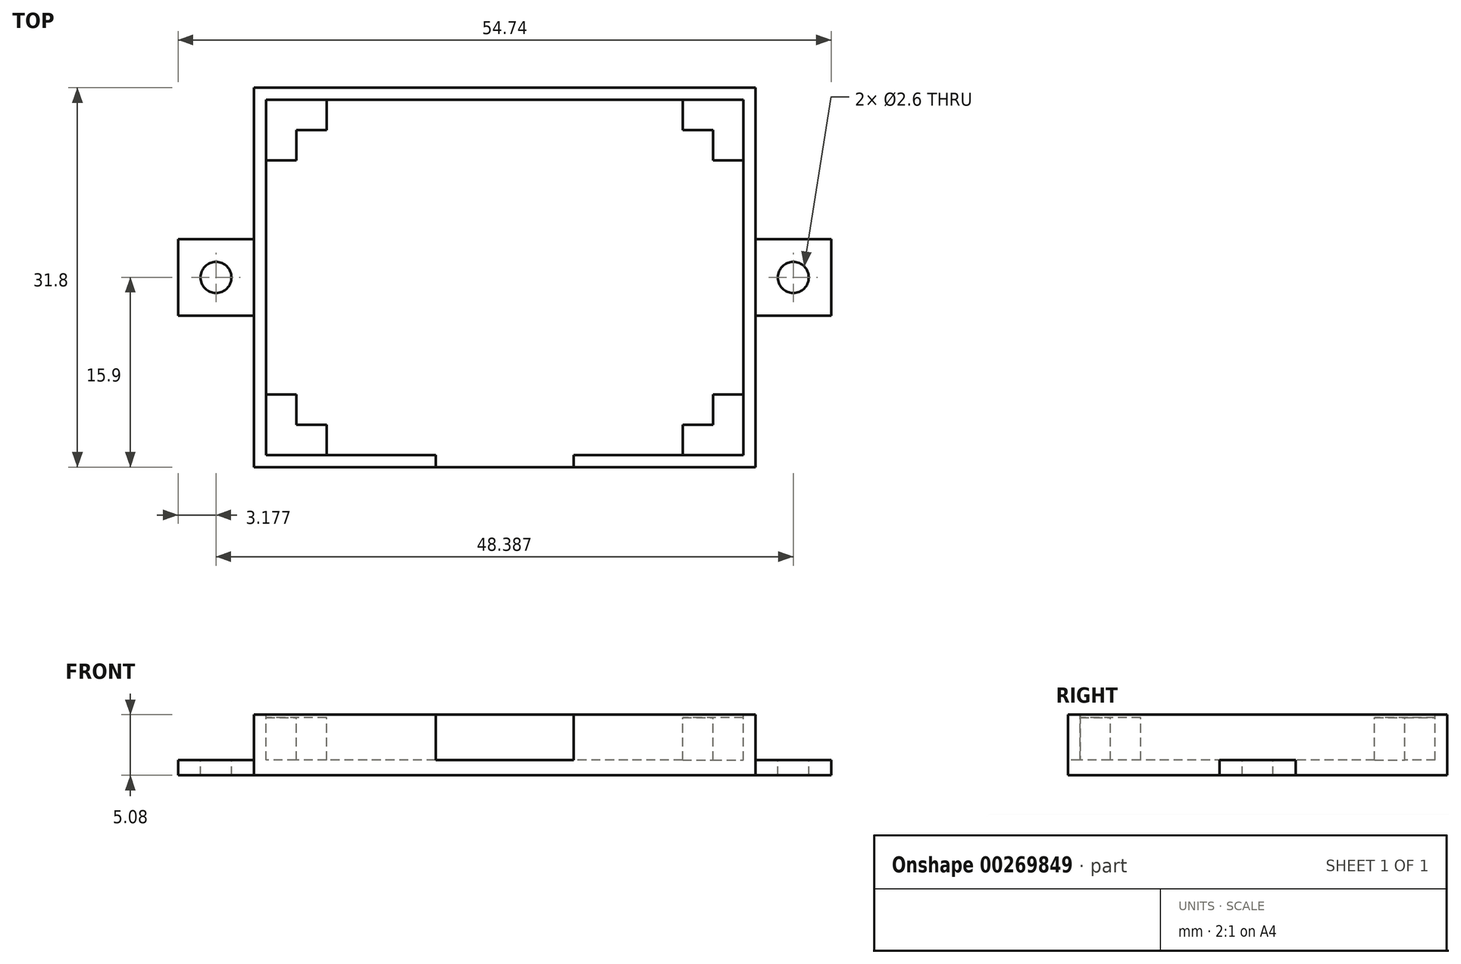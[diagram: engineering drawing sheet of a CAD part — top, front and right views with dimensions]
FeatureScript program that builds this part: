
annotation { "Feature Type Name" : "Feature", "Feature Type Description" : "" }
export const myFeature = defineFeature(function(context is Context, id is Id, definition is map)
    precondition{}
    {
        {
            var Q0;
            Q0=qCreatedBy(makeId("Top.planeOp"),FACE);
            var sketch = newSketch(context, id + "F0", { "sketchPlane" : qUnion([Q0])});
            skLineSegment(sketch, "E0.bottom", {"start": v(21.02, 15.9) * mm, "end": v(-21.02, 15.9) * mm});
            skLineSegment(sketch, "E0.top", {"start": v(21.02, -15.9) * mm, "end": v(-21.02, -15.9) * mm});
            skLineSegment(sketch, "E0.left", {"start": v(21.02, 15.9) * mm, "end": v(21.02, -15.9) * mm});
            skLineSegment(sketch, "E0.right", {"start": v(-21.02, 15.9) * mm, "end": v(-21.02, -15.9) * mm});
            skPoint(sketch, "E0.middle", {"position": v(0, 0) * mm});
            skSolve(sketch);
        }
        {
            var Q0;
            Q0 = qSketchRegion(id + "F0", true);
            extrude(context, id + "F1", {"entities" : qUnion([Q0]), "depth" : 5.08 * mm});
        }
        {
            var Q0;
            Q0=makeQuery(id+"F1.opExtrude","CAP_FACE",FACE,{"disambiguationData":[OSD([sQuery(id+"F0.wireOp",EDGE,"E0.bottom"),sQuery(id+"F0.wireOp",EDGE,"E0.top"),sQuery(id+"F0.wireOp",EDGE,"E0.left"),sQuery(id+"F0.wireOp",EDGE,"E0.right")])],"isStart":false});
            var sketch = newSketch(context, id + "F2", { "sketchPlane" : qUnion([Q0])});
            skLineSegment(sketch, "E1.bottom", {"start": v(20, 14.88) * mm, "end": v(-20, 14.88) * mm});
            skLineSegment(sketch, "E1.top", {"start": v(20, -14.88) * mm, "end": v(-20, -14.88) * mm});
            skLineSegment(sketch, "E1.left", {"start": v(20, 14.88) * mm, "end": v(20, -14.88) * mm});
            skLineSegment(sketch, "E1.right", {"start": v(-20, 14.88) * mm, "end": v(-20, -14.88) * mm});
            skPoint(sketch, "E1.middle", {"position": v(0, 0) * mm});
            skSolve(sketch);
        }
        {
            var Q0;
            Q0 = qSketchRegion(id + "F2", true);
            extrude(context, id + "F3", {"entities" : qUnion([Q0]), "operationType" : NewBodyOperationType.REMOVE, "oppositeDirection" : true, "depth" : 3.8 * mm});
        }
        {
            var Q0;
            Q0=makeQuery(id+"F3.boolean.opBoolean","COPY",FACE,{"derivedFrom":makeQuery(id+"F3.opExtrude","SWEPT_FACE",FACE,{"disambiguationData":[OSD([sQuery(id+"F2.wireOp",EDGE,"E1.bottom")])]})});
            var sketch = newSketch(context, id + "F4", { "sketchPlane" : qUnion([Q0])});
            skLineSegment(sketch, "E2.bottom", {"start": v(-20, 1.27) * mm, "end": v(-17.46, 1.27) * mm});
            skLineSegment(sketch, "E2.top", {"start": v(-20, 4.83) * mm, "end": v(-17.46, 4.83) * mm});
            skLineSegment(sketch, "E2.left", {"start": v(-20, 1.27) * mm, "end": v(-20, 4.83) * mm});
            skLineSegment(sketch, "E2.right", {"start": v(-17.46, 1.27) * mm, "end": v(-17.46, 4.83) * mm});
            skSolve(sketch);
        }
        {
            var Q0;
            Q0 = qSketchRegion(id + "F4", true);
            extrude(context, id + "F5", {"entities" : qUnion([Q0]), "operationType" : NewBodyOperationType.ADD, "depth" : 5.08 * mm});
        }
        {
            var Q0;
            Q0=makeQuery(id+"F5.opExtrude","SWEPT_FACE",FACE,{"disambiguationData":[OSD([sQuery(id+"F4.wireOp",EDGE,"E2.right")])]});
            var sketch = newSketch(context, id + "F6", { "sketchPlane" : qUnion([Q0])});
            skLineSegment(sketch, "E3.bottom", {"start": v(14.88, 1.27) * mm, "end": v(12.34, 1.27) * mm});
            skLineSegment(sketch, "E3.top", {"start": v(14.88, 4.83) * mm, "end": v(12.34, 4.83) * mm});
            skLineSegment(sketch, "E3.left", {"start": v(14.88, 1.27) * mm, "end": v(14.88, 4.83) * mm});
            skLineSegment(sketch, "E3.right", {"start": v(12.34, 1.27) * mm, "end": v(12.34, 4.83) * mm});
            skSolve(sketch);
        }
        {
            var Q0;
            Q0 = qSketchRegion(id + "F6", true);
            extrude(context, id + "F7", {"entities" : qUnion([Q0]), "operationType" : NewBodyOperationType.ADD, "depth" : 2.54 * mm});
        }
        {
            var Q0;
            Q0=makeQuery(id+"F3.boolean.opBoolean","COPY",FACE,{"derivedFrom":makeQuery(id+"F3.opExtrude","SWEPT_FACE",FACE,{"disambiguationData":[OSD([sQuery(id+"F2.wireOp",EDGE,"E1.right")])]})});
            var sketch = newSketch(context, id + "F8", { "sketchPlane" : qUnion([Q0])});
            skLineSegment(sketch, "E4.bottom", {"start": v(-14.88, 1.27) * mm, "end": v(-12.34, 1.27) * mm});
            skLineSegment(sketch, "E4.top", {"start": v(-14.88, 4.83) * mm, "end": v(-12.34, 4.83) * mm});
            skLineSegment(sketch, "E4.left", {"start": v(-14.88, 1.27) * mm, "end": v(-14.88, 4.83) * mm});
            skLineSegment(sketch, "E4.right", {"start": v(-12.34, 1.27) * mm, "end": v(-12.34, 4.83) * mm});
            skSolve(sketch);
        }
        {
            var Q0;
            Q0 = qSketchRegion(id + "F8", true);
            extrude(context, id + "F9", {"entities" : qUnion([Q0]), "operationType" : NewBodyOperationType.ADD, "depth" : 5.08 * mm});
        }
        {
            var Q0;
            Q0=makeQuery(id+"F9.opExtrude","SWEPT_FACE",FACE,{"disambiguationData":[OSD([sQuery(id+"F8.wireOp",EDGE,"E4.right")])]});
            var sketch = newSketch(context, id + "F10", { "sketchPlane" : qUnion([Q0])});
            skLineSegment(sketch, "E5.bottom", {"start": v(20, 1.27) * mm, "end": v(17.46, 1.27) * mm});
            skLineSegment(sketch, "E5.top", {"start": v(20, 4.83) * mm, "end": v(17.46, 4.83) * mm});
            skLineSegment(sketch, "E5.left", {"start": v(20, 1.27) * mm, "end": v(20, 4.83) * mm});
            skLineSegment(sketch, "E5.right", {"start": v(17.46, 1.27) * mm, "end": v(17.46, 4.83) * mm});
            skSolve(sketch);
        }
        {
            var Q0;
            Q0 = qSketchRegion(id + "F10", true);
            extrude(context, id + "F11", {"entities" : qUnion([Q0]), "operationType" : NewBodyOperationType.ADD, "depth" : 2.54 * mm});
        }
        {
            var Q0;
            Q0=makeQuery(id+"F3.boolean.opBoolean","COPY",FACE,{"derivedFrom":makeQuery(id+"F3.opExtrude","SWEPT_FACE",FACE,{"disambiguationData":[OSD([sQuery(id+"F2.wireOp",EDGE,"E1.top")])]})});
            var sketch = newSketch(context, id + "F12", { "sketchPlane" : qUnion([Q0])});
            skLineSegment(sketch, "E6.bottom", {"start": v(-20, 1.27) * mm, "end": v(-17.46, 1.27) * mm});
            skLineSegment(sketch, "E6.top", {"start": v(-20, 4.83) * mm, "end": v(-17.46, 4.83) * mm});
            skLineSegment(sketch, "E6.left", {"start": v(-20, 1.27) * mm, "end": v(-20, 4.83) * mm});
            skLineSegment(sketch, "E6.right", {"start": v(-17.46, 1.27) * mm, "end": v(-17.46, 4.83) * mm});
            skSolve(sketch);
        }
        {
            var Q0;
            Q0 = qSketchRegion(id + "F12", true);
            extrude(context, id + "F13", {"entities" : qUnion([Q0]), "operationType" : NewBodyOperationType.ADD, "depth" : 5.08 * mm});
        }
        {
            var Q0;
            Q0=makeQuery(id+"F13.opExtrude","SWEPT_FACE",FACE,{"disambiguationData":[OSD([sQuery(id+"F12.wireOp",EDGE,"E6.right")])]});
            var sketch = newSketch(context, id + "F14", { "sketchPlane" : qUnion([Q0])});
            skLineSegment(sketch, "E7.bottom", {"start": v(14.88, 1.27) * mm, "end": v(12.34, 1.27) * mm});
            skLineSegment(sketch, "E7.top", {"start": v(14.88, 4.83) * mm, "end": v(12.34, 4.83) * mm});
            skLineSegment(sketch, "E7.left", {"start": v(14.88, 1.27) * mm, "end": v(14.88, 4.83) * mm});
            skLineSegment(sketch, "E7.right", {"start": v(12.34, 1.27) * mm, "end": v(12.34, 4.83) * mm});
            skSolve(sketch);
        }
        {
            var Q0;
            Q0 = qSketchRegion(id + "F14", true);
            extrude(context, id + "F15", {"entities" : qUnion([Q0]), "operationType" : NewBodyOperationType.ADD, "depth" : 2.54 * mm});
        }
        {
            var Q0;
            Q0=makeQuery(id+"F3.boolean.opBoolean","COPY",FACE,{"derivedFrom":makeQuery(id+"F3.opExtrude","SWEPT_FACE",FACE,{"disambiguationData":[OSD([sQuery(id+"F2.wireOp",EDGE,"E1.left")])]})});
            var sketch = newSketch(context, id + "F16", { "sketchPlane" : qUnion([Q0])});
            skLineSegment(sketch, "E8.bottom", {"start": v(-14.88, 1.27) * mm, "end": v(-12.34, 1.27) * mm});
            skLineSegment(sketch, "E8.top", {"start": v(-14.88, 4.83) * mm, "end": v(-12.34, 4.83) * mm});
            skLineSegment(sketch, "E8.left", {"start": v(-14.88, 1.27) * mm, "end": v(-14.88, 4.83) * mm});
            skLineSegment(sketch, "E8.right", {"start": v(-12.34, 1.27) * mm, "end": v(-12.34, 4.83) * mm});
            skSolve(sketch);
        }
        {
            var Q0;
            Q0 = qSketchRegion(id + "F16", true);
            extrude(context, id + "F17", {"entities" : qUnion([Q0]), "operationType" : NewBodyOperationType.ADD, "depth" : 5.08 * mm});
        }
        {
            var Q0;
            Q0=makeQuery(id+"F17.opExtrude","SWEPT_FACE",FACE,{"disambiguationData":[OSD([sQuery(id+"F16.wireOp",EDGE,"E8.right")])]});
            var sketch = newSketch(context, id + "F18", { "sketchPlane" : qUnion([Q0])});
            skLineSegment(sketch, "E9.bottom", {"start": v(20, 1.27) * mm, "end": v(17.46, 1.27) * mm});
            skLineSegment(sketch, "E9.top", {"start": v(20, 4.83) * mm, "end": v(17.46, 4.83) * mm});
            skLineSegment(sketch, "E9.left", {"start": v(20, 1.27) * mm, "end": v(20, 4.83) * mm});
            skLineSegment(sketch, "E9.right", {"start": v(17.46, 1.27) * mm, "end": v(17.46, 4.83) * mm});
            skSolve(sketch);
        }
        {
            var Q0;
            Q0 = qSketchRegion(id + "F18", true);
            extrude(context, id + "F19", {"entities" : qUnion([Q0]), "operationType" : NewBodyOperationType.ADD, "depth" : 2.54 * mm});
        }
        {
            var Q0;
            Q0=makeQuery(id+"F1.opExtrude","SWEPT_FACE",FACE,{"disambiguationData":[OSD([sQuery(id+"F0.wireOp",EDGE,"E0.top")])]});
            var sketch = newSketch(context, id + "F20", { "sketchPlane" : qUnion([Q0])});
            skLineSegment(sketch, "E10.bottom", {"start": v(-5.78, 5.08) * mm, "end": v(5.78, 5.08) * mm});
            skLineSegment(sketch, "E10.top", {"start": v(-5.78, 1.27) * mm, "end": v(5.78, 1.27) * mm});
            skLineSegment(sketch, "E10.left", {"start": v(-5.78, 5.08) * mm, "end": v(-5.78, 1.27) * mm});
            skLineSegment(sketch, "E10.right", {"start": v(5.78, 5.08) * mm, "end": v(5.78, 1.27) * mm});
            skSolve(sketch);
        }
        {
            var Q0;
            Q0 = qSketchRegion(id + "F20", true);
            extrude(context, id + "F21", {"entities" : qUnion([Q0]), "operationType" : NewBodyOperationType.REMOVE, "endBound" : BoundingType.UP_TO_NEXT, "oppositeDirection" : true, "depth" : 25.4 * mm});
        }
        {
            var Q0;
            Q0=makeQuery(id+"F1.opExtrude","SWEPT_FACE",FACE,{"disambiguationData":[OSD([sQuery(id+"F0.wireOp",EDGE,"E0.left")])]});
            var sketch = newSketch(context, id + "F22", { "sketchPlane" : qUnion([Q0])});
            skLineSegment(sketch, "E11.bottom", {"start": v(-3.2, 0) * mm, "end": v(3.2, 0) * mm});
            skLineSegment(sketch, "E11.top", {"start": v(-3.2, 1.27) * mm, "end": v(3.2, 1.27) * mm});
            skLineSegment(sketch, "E11.left", {"start": v(-3.2, 0) * mm, "end": v(-3.2, 1.27) * mm});
            skLineSegment(sketch, "E11.right", {"start": v(3.2, 0) * mm, "end": v(3.2, 1.27) * mm});
            skSolve(sketch);
        }
        {
            var Q0;
            Q0 = qSketchRegion(id + "F22", true);
            extrude(context, id + "F23", {"entities" : qUnion([Q0]), "operationType" : NewBodyOperationType.ADD, "depth" : 6.35 * mm});
        }
        {
            var Q0;
            Q0=makeQuery(id+"F1.opExtrude","SWEPT_FACE",FACE,{"disambiguationData":[OSD([sQuery(id+"F0.wireOp",EDGE,"E0.right")])]});
            var sketch = newSketch(context, id + "F24", { "sketchPlane" : qUnion([Q0])});
            skLineSegment(sketch, "E12.bottom", {"start": v(-3.2, 0) * mm, "end": v(3.2, 0) * mm});
            skLineSegment(sketch, "E12.top", {"start": v(-3.2, 1.27) * mm, "end": v(3.2, 1.27) * mm});
            skLineSegment(sketch, "E12.left", {"start": v(-3.2, 0) * mm, "end": v(-3.2, 1.27) * mm});
            skLineSegment(sketch, "E12.right", {"start": v(3.2, 0) * mm, "end": v(3.2, 1.27) * mm});
            skSolve(sketch);
        }
        {
            var Q0;
            Q0 = qSketchRegion(id + "F24", true);
            extrude(context, id + "F25", {"entities" : qUnion([Q0]), "operationType" : NewBodyOperationType.ADD, "depth" : 6.35 * mm});
        }
        {
            var Q0;
            Q0=makeQuery(id+"F23.opExtrude","SWEPT_FACE",FACE,{"disambiguationData":[OSD([sQuery(id+"F22.wireOp",EDGE,"E11.top")])]});
            var sketch = newSketch(context, id + "F26", { "sketchPlane" : qUnion([Q0])});
            skCircle(sketch, "E13", {"center": v(24.2, 0) * mm, "radius": 1.3 * mm});
            skPoint(sketch, "E13.centerSnap0", {"position": v(21.02, 0) * mm});
            skPoint(sketch, "E13.centerSnap1", {"position": v(24.2, -3.2) * mm});
            skSolve(sketch);
        }
        {
            var Q0;
            Q0 = qSketchRegion(id + "F26", true);
            extrude(context, id + "F27", {"entities" : qUnion([Q0]), "operationType" : NewBodyOperationType.REMOVE, "endBound" : BoundingType.THROUGH_ALL, "oppositeDirection" : true, "depth" : 25.4 * mm});
        }
        {
            var Q0;
            Q0=makeQuery(id+"F25.opExtrude","SWEPT_FACE",FACE,{"disambiguationData":[OSD([sQuery(id+"F24.wireOp",EDGE,"E12.top")])]});
            var sketch = newSketch(context, id + "F28", { "sketchPlane" : qUnion([Q0])});
            skCircle(sketch, "E14", {"center": v(-24.2, 0) * mm, "radius": 1.3 * mm});
            skPoint(sketch, "E14.centerSnap0", {"position": v(-24.2, 3.2) * mm});
            skSolve(sketch);
        }
        {
            var Q0;
            Q0 = qSketchRegion(id + "F28", true);
            extrude(context, id + "F29", {"entities" : qUnion([Q0]), "operationType" : NewBodyOperationType.REMOVE, "endBound" : BoundingType.UP_TO_NEXT, "oppositeDirection" : true, "depth" : 25.4 * mm});
        }
    });
